# Revit family: PRD_FrankeWS_ShwrMxrs_SelfClosingShowerMixer_F3SM2001,2002
name_source: partatom
category: Plumbing Fixtures
revit_build: Autodesk Revit 2018 (Build: 20190510_1515(x64)
units: mm (PartAtom-declared; Revit-internal decimal feet)

## family parameters
Cut with Voids When Loaded = No
Host = Face
OmniClass Number = 23.45.05.14.99
OmniClass Title = Other Sanitary Washing Plumbing Fixtures
Part Type = Normal
Room Calculation Point = No
Round Connector Dimension = Use Diameter
Shared = No

## types (2) — shared parameters
AdditionalConnections = no
AdjustableFlowTime = yes
AssetType = Fixed
Category = Pr_40_20_87_78, Shower manual water supply sets
Circulation = no
CloseOffRating = 0.0 Pa
Color = Chrome
ConnectionWithPayWaterDispenser = not possible
Default Elevation = 850 mm  [stored 2.78871 ft]
DiameterNominal = 15.000 mm
DurationUnit = year
Features = For shower facilities. Connects to hot and cold water, high-polished chromium-plated brass.
Finish = high-polished chromium-plated brass
FlowCoefficient = 0
FlowColdWater = 0.2 L/s
FlowHotWater = 0.2 L/s
FunctionalPrinciple = hydraulic self-closing
GrossWeight = 2.30 kg
HygieneFlushing = no
IfcExportAs = IfcValveType
IfcExportType = MIXING
InletSize = G-1-2-B
Manufacturer = KWC Group AG
ManufacturerName = KWC Group AG
ManufacturerURL = www.kwc.com
Material = Brass
MaterialsBody = Brass
MaximumFlowTime = 35.00 seconds
MinimumFlowPressure = 1.00 bar
MinimumFlowTime = 5.00 seconds
MixerControl = Other
NBSDescription = Shower manual water supply sets
NBSReference = 45-35-70/335
NetWeight = 2.00 kg
NominalWidth = 202 mm  [stored 0.66273 ft]
OutletConnectionSize = 15 mm  [stored 0.0492126 ft]
PositionOfWaterConnection = from backside
ProductInformation = https://pim.kwc.com
ProtectiveShutdown = no
ShowerPipeDraining = no
TapMaterial = PRD_AR_ChromatedBrass_HighPolished
TestPressure = 0.0 Pa
ThermalDisinfection = no
TypeOfMixing = with mixer
TypeOfMounting = Wall mounting
TypeOfOperation = manual operation
TypeOfShower = wall fitting
URL = www.kwc.com
Uniclass2015Code = Pr_40_20_87_78
Uniclass2015Title = Shower manual water supply sets
Uniclass2015Version = Products v1.10
ValveMechanism = Other
ValveOperation = Other
ValvePattern = ANGLED_2_PORT
Version = 1
VolumeFlowRate = 0.25 L/s at 3 bar
WarrantyDurationUnit = year
zero-valued in all types: NominalHeight, NominalLength

## per-type parameters (varying)
| type | BIMObjectName | Description | Model | ModelNumber | ModelReference | Name | OutletBottom | OutletTop |
| F3SM2001 - 0.25 L/s, top outlet | PRD_AR_ShowerMixers_SelfClosingShowerMixer_F3SM2001 | F3S-Mix self-closing wall-mounted mixer DN 15 as single-mixer for wall mounting, for shower facilities. Self-closing mixing cartridge, hydraulically controlled, piston-free design, self-closing, stepless configuration of flow duration. With adjustable temperature stop. Connects to hot and cold water. Housing with outlet on top, G 3/4 B, for installation of bent outlet or surface-mounted shower pipe, high-polished chromium-plated brass. With adjustable connections, with backflow preventer, strainers and screw rosettes. | F3SM2001 | 2030036198 | F3SM2001 | F3 self-closing shower mixer F3SM2001 | No | Yes |
| F3SM2002 - 0.25 L/s, bottom outlet | PRD_AR_ShowerMixers_SelfClosingShowerMixer_F3SM2002 | F3S-Mix self-closing wall-mounted mixer DN 15 as single-mixer for wall mounting, for shower facilities. Self-closing mixing cartridge, hydraulically controlled, piston-free design, self-closing, stepless configuration of flow duration. With adjustable temperature stop. Connects to hot and cold water. Housing with hand shower connection G 1/2 B, high-polished chromium-plated brass. With adjustable connections, with backflow preventer, strainers and screw rosettes. | F3SM2002 | 2030036202 | F3SM2002 | F3 self-closing shower mixer F3SM2002 | Yes | No |

note: [stored X ft] marks values corroborated as IEEE doubles in the binary element streams (Revit-internal decimal feet)

## geometry (parser evidence)
native form markers: Sweep x2
no freeform markers — native parametric forms only
